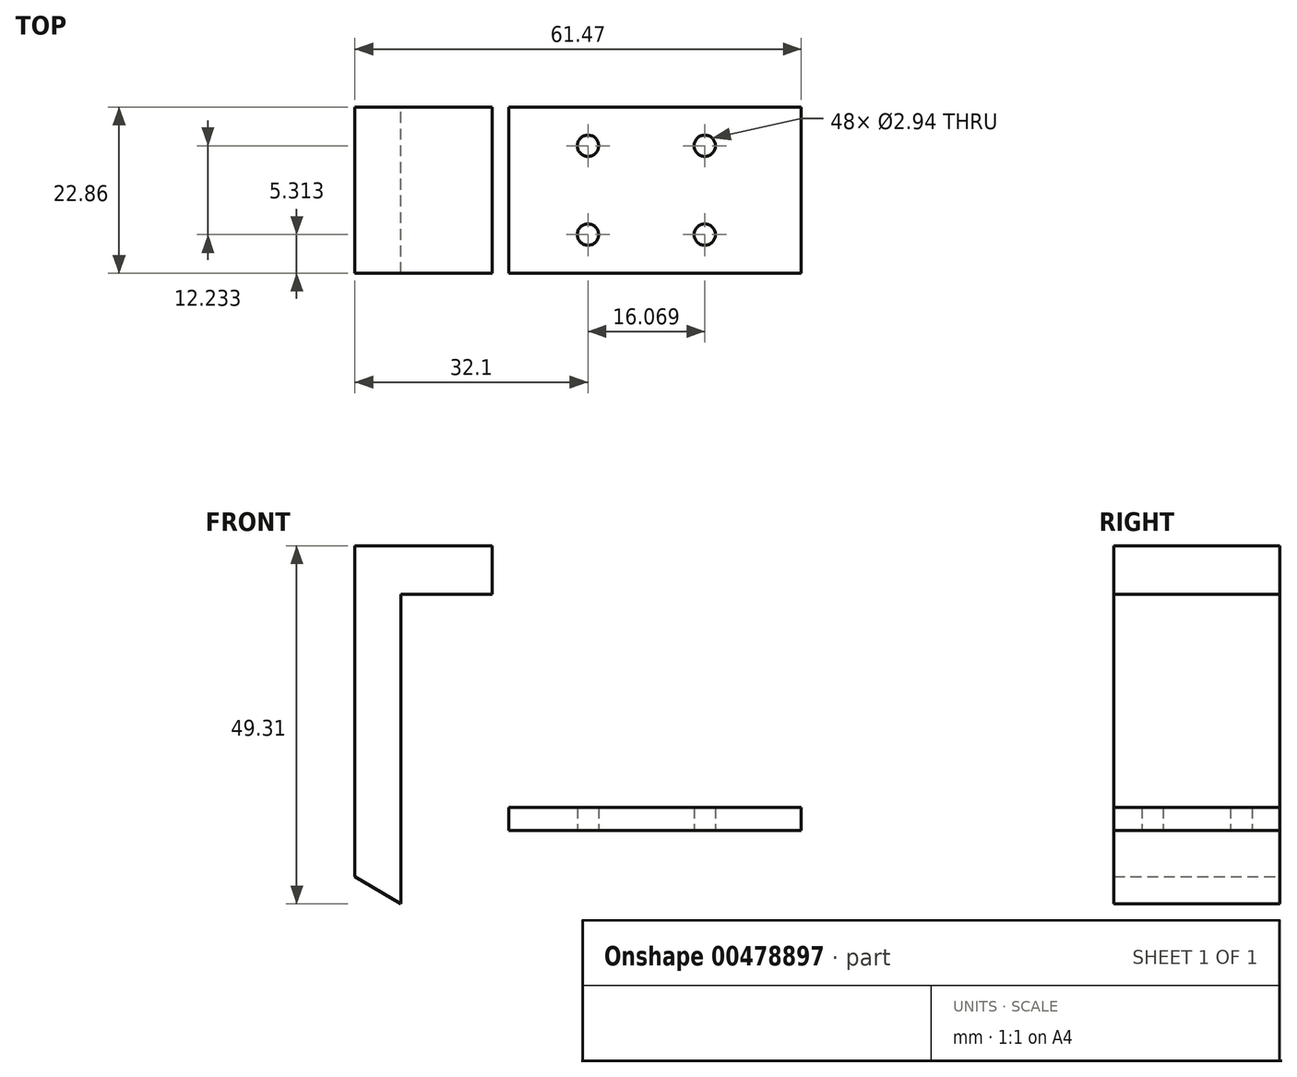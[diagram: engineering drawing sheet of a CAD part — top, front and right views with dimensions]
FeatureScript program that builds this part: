
annotation { "Feature Type Name" : "Feature", "Feature Type Description" : "" }
export const myFeature = defineFeature(function(context is Context, id is Id, definition is map)
    precondition{}
    {
        {
            var Q0;
            Q0=qCreatedBy(makeId("Front.planeOp"),FACE);
            var sketch = newSketch(context, id + "F0", { "sketchPlane" : qUnion([Q0])});
            skLineSegment(sketch, "E0.bottom", {"start": v(40.25, -4.43) * mm, "end": v(0, -4.43) * mm});
            skLineSegment(sketch, "E0.top", {"start": v(40.25, -1.26) * mm, "end": v(0, -1.26) * mm});
            skLineSegment(sketch, "E0.left", {"start": v(40.25, -1.26) * mm, "end": v(40.25, -4.43) * mm});
            skLineSegment(sketch, "E0.right", {"start": v(0, -1.26) * mm, "end": v(0, -4.43) * mm});
            skLineSegment(sketch, "E1", {"start": v(-2.24, 0) * mm, "end": v(-2.24, 28.1) * mm});
            skLineSegment(sketch, "E2", {"start": v(-2.24, 28.1) * mm, "end": v(-14.87, 28.1) * mm});
            skLineSegment(sketch, "E3", {"start": v(-21.22, -10.78) * mm, "end": v(-21.22, 28.1) * mm});
            skLineSegment(sketch, "E4", {"start": v(-23.6, 28.63) * mm, "end": v(-23.6, -20.2) * mm});
            skLineSegment(sketch, "E5", {"start": v(-12.1, 4.1) * mm, "end": v(-12.12, -20.2) * mm});
            skLineSegment(sketch, "E6", {"start": v(-21.22, -10.78) * mm, "end": v(-14.87, -14.52) * mm});
            skLineSegment(sketch, "E7", {"start": v(-14.87, 28.1) * mm, "end": v(-14.87, -14.52) * mm});
            skLineSegment(sketch, "E8", {"start": v(-12.18, -0.37) * mm, "end": v(-12.18, 4.1) * mm});
            skArc(sketch, "E9", {"start": v(-21.22, 28.1) * mm, "mid": v(-22.07, 29.84) * mm, "end": v(-23.6, 28.63) * mm});
            skArc(sketch, "E10", {"start": v(-23.6, -20.2) * mm, "mid": v(-17.86, -22.22) * mm, "end": v(-12.12, -20.2) * mm});
            skArc(sketch, "E11", {"start": v(-2.24, 0) * mm, "mid": v(-1.49, -1.28) * mm, "end": v(0, -1.26) * mm});
            skArc(sketch, "E12.0", {"start": v(-5.41, 0) * mm, "mid": v(-3.9, -3.43) * mm, "end": v(-0.33, -4.63) * mm});
            skLineSegment(sketch, "E13.bottom", {"start": v(-21.22, 28.1) * mm, "end": v(-2.34, 28.1) * mm});
            skLineSegment(sketch, "E13.top", {"start": v(-21.22, 34.8) * mm, "end": v(-2.34, 34.8) * mm});
            skLineSegment(sketch, "E13.left", {"start": v(-21.22, 28.1) * mm, "end": v(-21.22, 34.8) * mm});
            skLineSegment(sketch, "E13.right", {"start": v(-2.34, 28.1) * mm, "end": v(-2.34, 34.8) * mm});
            skSolve(sketch);
        }
        {
            var Q0;
            Q0 = qSketchRegion(id + "F0", true);
            extrude(context, id + "F1", {"entities" : qUnion([Q0]), "depth" : 22.86 * mm, "offsetDistance" : 25.4 * mm});
        }
        {
            var Q0;
            Q0=makeQuery(id+"F1.opExtrude","SWEPT_FACE",FACE,{"disambiguationData":[OSD([sQuery(id+"F0.wireOp",EDGE,"E0.bottom"),sQuery(id+"F0.wireOp",EDGE,"xof8F0UG-0jiF-Eeqd-ck1P-6GOrIFrXYfqs.bottom")])]});
            var sketch = newSketch(context, id + "F2", { "sketchPlane" : qUnion([Q0])});
            skCircle(sketch, "E14", {"center": v(10.88, 17.55) * mm, "radius": 1.47 * mm});
            skLineSegment(sketch, "E15", {"start": v(-3.18, 11.43) * mm, "end": v(40.25, 11.43) * mm});
            skLineSegment(sketch, "E16", {"start": v(18.91, 0) * mm, "end": v(18.91, 11.43) * mm});
            skLineSegment(sketch, "E17", {"start": v(18.91, 22.86) * mm, "end": v(18.91, 0) * mm});
            skCircle(sketch, "E18.MirrorC", {"center": v(26.95, 17.55) * mm, "radius": 1.47 * mm});
            skLineSegment(sketch, "E19.MirrorCS", {"start": v(41, 11.43) * mm, "end": v(-2.42, 11.43) * mm});
            skCircle(sketch, "E20.MirrorC", {"center": v(10.88, 5.31) * mm, "radius": 1.47 * mm});
            skCircle(sketch, "E21.MirrorC", {"center": v(26.95, 5.31) * mm, "radius": 1.47 * mm});
            skSolve(sketch);
        }
        {
            var Q0;
            Q0 = qSketchRegion(id + "F2", true);
            extrude(context, id + "F3", {"entities" : qUnion([Q0]), "operationType" : NewBodyOperationType.REMOVE, "oppositeDirection" : true, "depth" : 25.4 * mm});
        }
    });
